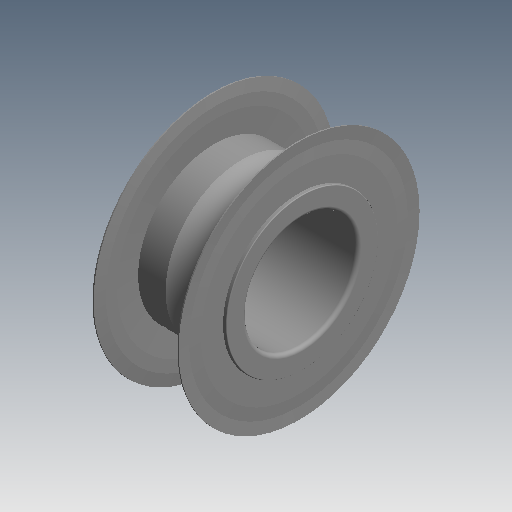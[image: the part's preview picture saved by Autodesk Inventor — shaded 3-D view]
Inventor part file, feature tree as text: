
AUTODESK INVENTOR PART (.ipt)
format: ipt  version: 2020 (Build 240168000, 168)  size: 192,000 bytes
history: native  units: mm (DEFAULTED — no unit token found)
features: revolve x3, sketch x3
ambient origin geometry x8: Origin, YZ Plane, XZ Plane, XY Plane, X Axis, Y Axis, Z Axis, Center Point
bodies: Solid1 (feature_tree)
feature tree (6):
  revolve  "Revolution1"  Angle=360.0deg
  revolve  "Revolution2"  [1 undecoded]
  revolve  "Revolution3"  [1 undecoded]
  sketch  "Sketch_17"  dims[d0=360.0deg d1=360.0deg]
  sketch  "Sketch_20"  dims[d2=360.0deg]
  sketch  "Sketch_21"
note: 2 required parameter values undecoded (feature->parameter linkage not recoverable at this tier; creation-order binding heuristic only, values carry confidence <= 0.55)
